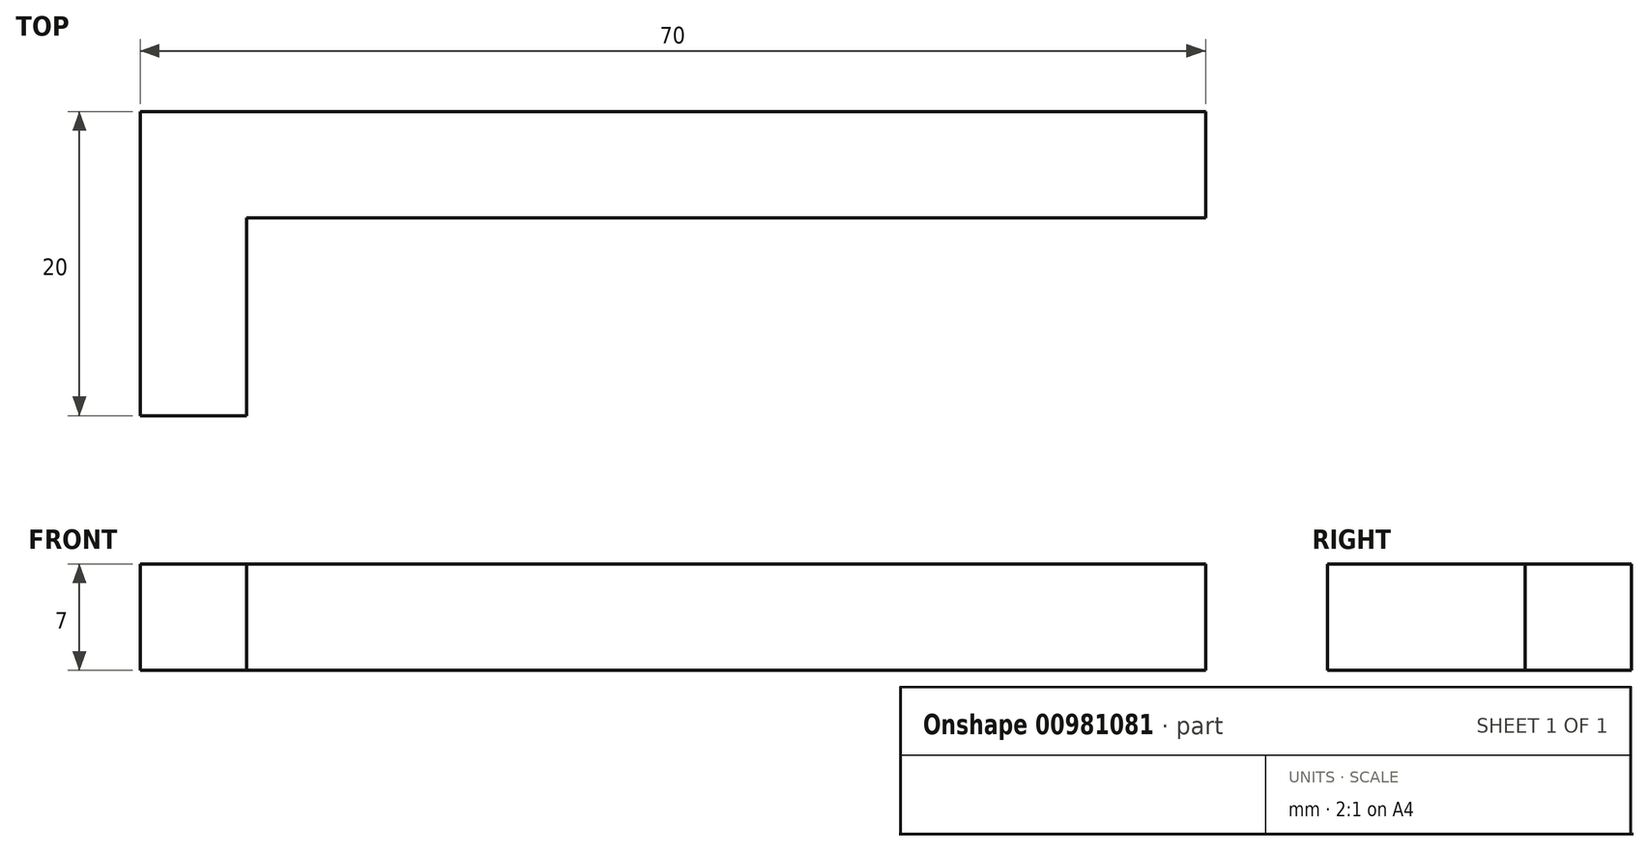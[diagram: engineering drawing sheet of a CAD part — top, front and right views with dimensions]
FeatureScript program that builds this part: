
annotation { "Feature Type Name" : "Feature", "Feature Type Description" : "" }
export const myFeature = defineFeature(function(context is Context, id is Id, definition is map)
    precondition{}
    {
        {
            var Q0;
            Q0=qCreatedBy(makeId("Top.planeOp"),FACE);
            var sketch = newSketch(context, id + "F0", { "sketchPlane" : qUnion([Q0])});
            skLineSegment(sketch, "E0.bottom", {"start": v(-47.36, 6.73) * mm, "end": v(22.64, 6.73) * mm});
            skLineSegment(sketch, "E0.top", {"start": v(-40.36, -0.27) * mm, "end": v(22.64, -0.27) * mm});
            skLineSegment(sketch, "E0.right", {"start": v(22.64, 6.73) * mm, "end": v(22.64, -0.27) * mm});
            skLineSegment(sketch, "E1.top", {"start": v(-47.36, -13.27) * mm, "end": v(-40.36, -13.27) * mm});
            skLineSegment(sketch, "E1.right", {"start": v(-40.36, -0.27) * mm, "end": v(-40.36, -13.27) * mm});
            skLineSegment(sketch, "E2", {"start": v(-47.36, -13.27) * mm, "end": v(-47.36, 6.73) * mm});
            skSolve(sketch);
        }
        {
            var Q0;
            Q0 = qSketchRegion(id + "F0", true);
            extrude(context, id + "F1", {"entities" : qUnion([Q0]), "depth" : 7 * mm, "offsetDistance" : 25 * mm});
        }
    });
